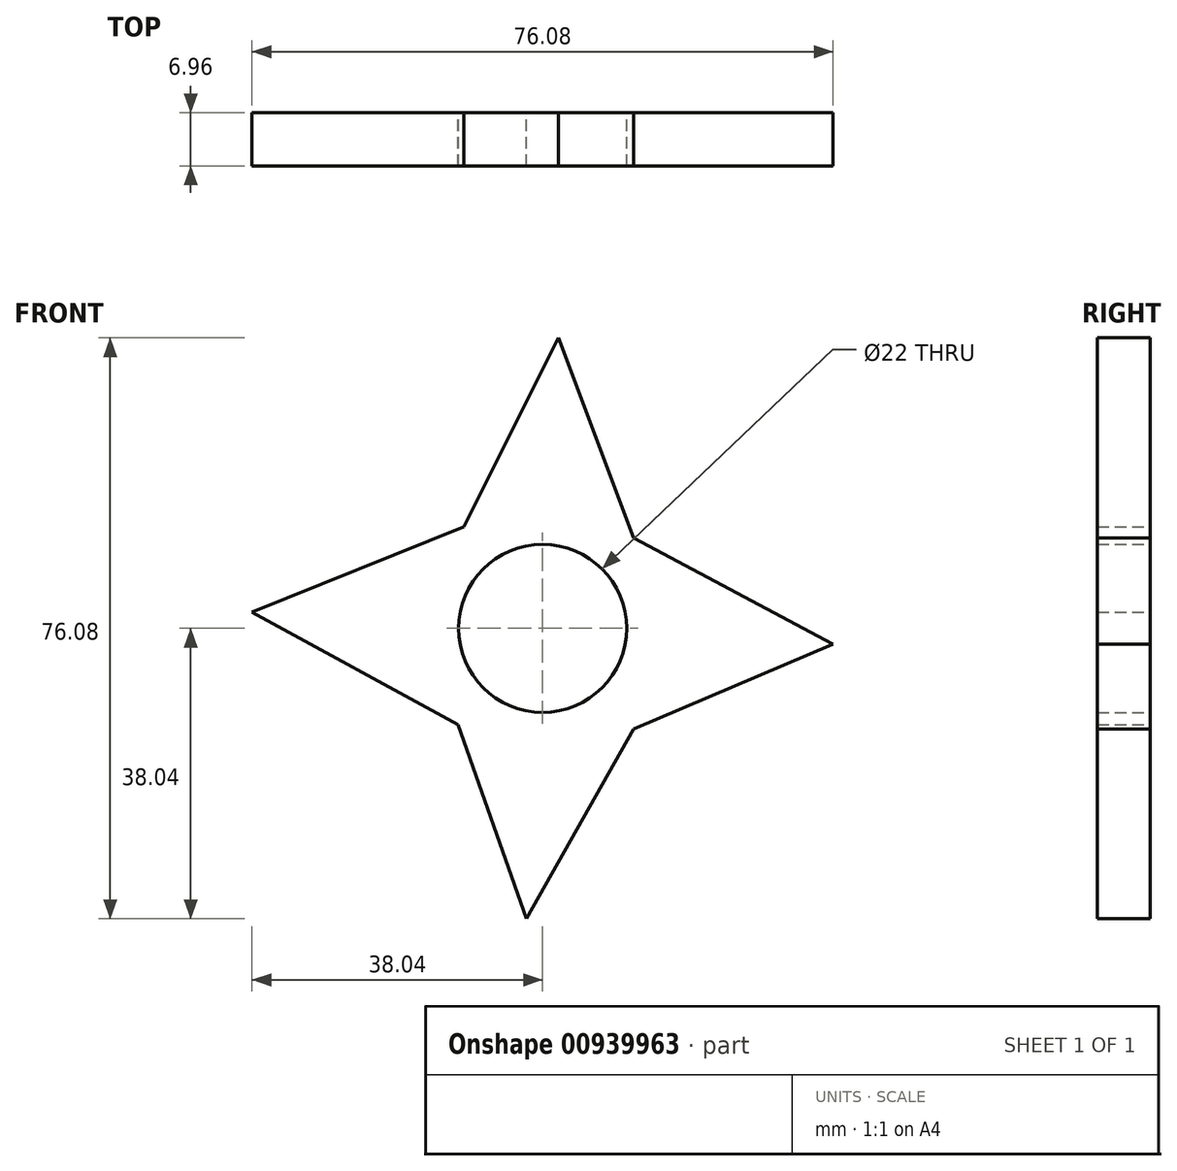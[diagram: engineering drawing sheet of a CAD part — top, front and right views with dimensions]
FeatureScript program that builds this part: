
annotation { "Feature Type Name" : "Feature", "Feature Type Description" : "" }
export const myFeature = defineFeature(function(context is Context, id is Id, definition is map)
    precondition{}
    {
        {
            var Q0;
            Q0=qCreatedBy(makeId("Front.planeOp"),FACE);
            var sketch = newSketch(context, id + "F0", { "sketchPlane" : qUnion([Q0])});
            skLineSegment(sketch, "E0", {"start": v(-55.39, 64.86) * mm, "end": v(-55.45, 64.92) * mm});
            skArc(sketch, "E1", {"start": v(0, 0.09) * mm, "mid": v(-0.06, 0.06) * mm, "end": v(-0.09, 0) * mm});
            skCircle(sketch, "E2", {"center": v(0, 0) * mm, "radius": 0.04 * mm});
            skCircle(sketch, "E3", {"center": v(0, 0) * mm, "radius": 11 * mm});
            skPoint(sketch, "E4.0.midPoint", {"position": v(32.85, -36.68) * mm});
            skLineSegment(sketch, "E5", {"start": v(0, 0.09) * mm, "end": v(0, 0.04) * mm});
            skLineSegment(sketch, "E6", {"start": v(2.1, 38.04) * mm, "end": v(-10.28, 13.26) * mm});
            skLineSegment(sketch, "E7", {"start": v(-10.28, 13.26) * mm, "end": v(2.1, 38.04) * mm});
            skLineSegment(sketch, "E8", {"start": v(11.92, 11.81) * mm, "end": v(2.1, 38.04) * mm});
            skLineSegment(sketch, "E9", {"start": v(11.92, 11.81) * mm, "end": v(38.04, -2.1) * mm});
            skLineSegment(sketch, "E10", {"start": v(38.04, -2.1) * mm, "end": v(11.92, -13.17) * mm});
            skLineSegment(sketch, "E11", {"start": v(11.92, -13.17) * mm, "end": v(-2.1, -38.04) * mm});
            skLineSegment(sketch, "E12", {"start": v(-2.1, -38.04) * mm, "end": v(-11.04, -12.64) * mm});
            skLineSegment(sketch, "E13", {"start": v(-11.04, -12.64) * mm, "end": v(-38.04, 2.1) * mm});
            skLineSegment(sketch, "E14", {"start": v(-38.04, 2.1) * mm, "end": v(-10.28, 13.26) * mm});
            skPoint(sketch, "E15.orphan", {"position": v(69.53, -3.82) * mm});
            skLineSegment(sketch, "E16.trimOffspring", {"start": v(0.09, 0) * mm, "end": v(0, 0) * mm});
            skLineSegment(sketch, "E17.trimOffspring", {"start": v(-0.09, 0) * mm, "end": v(0, 0) * mm});
            skLineSegment(sketch, "E18.trimOffspring", {"start": v(0, -0.09) * mm, "end": v(0, 0) * mm});
            skPoint(sketch, "E19.start.orphan", {"position": v(-3.82, -69.53) * mm});
            skSolve(sketch);
        }
        {
            var Q0;
            Q0 = qSketchRegion(id + "F0", true);
            extrude(context, id + "F1", {"entities" : qUnion([Q0]), "depth" : 6.96 * mm, "offsetDistance" : 25 * mm});
        }
        {
            var Q0;
            Q0 = qSketchRegion(id + "F0", true);
            extrude(context, id + "F2", {"entities" : qUnion([Q0]), "operationType" : NewBodyOperationType.ADD, "depth" : 6.96 * mm, "offsetDistance" : 25 * mm});
        }
    });
